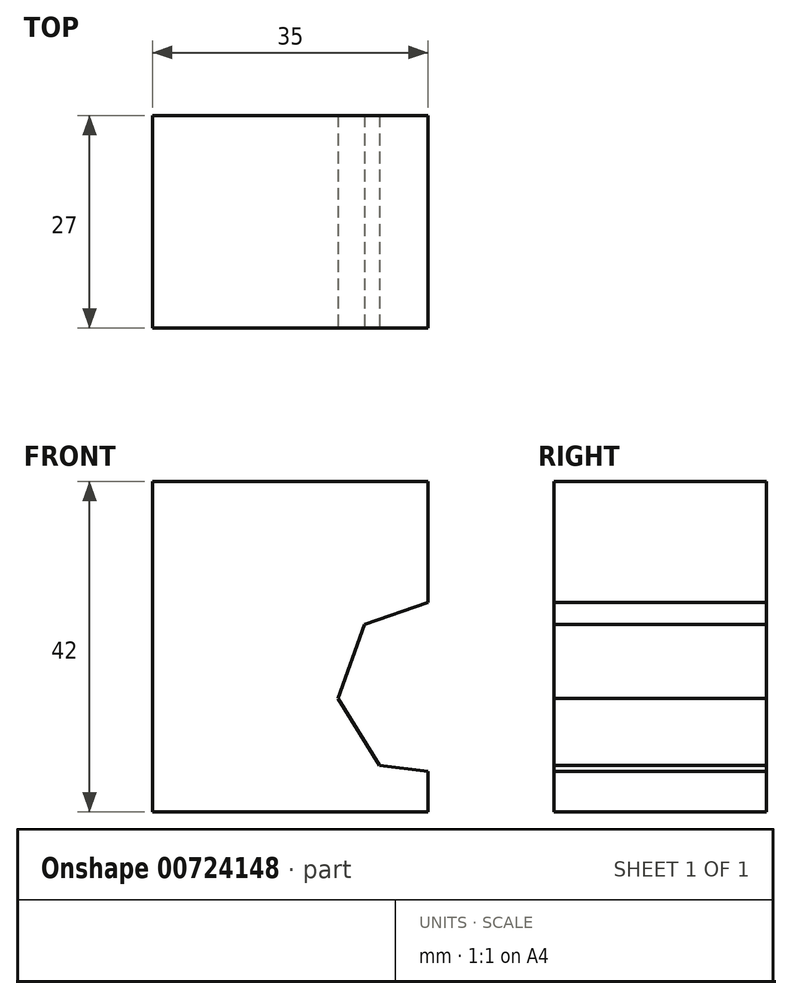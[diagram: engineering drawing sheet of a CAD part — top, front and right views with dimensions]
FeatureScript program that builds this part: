
annotation { "Feature Type Name" : "Feature", "Feature Type Description" : "" }
export const myFeature = defineFeature(function(context is Context, id is Id, definition is map)
    precondition{}
    {
        {
            var Q0;
            Q0=qCreatedBy(makeId("Front.planeOp"),FACE);
            var sketch = newSketch(context, id + "F0", { "sketchPlane" : qUnion([Q0])});
            skLineSegment(sketch, "E0.bottom", {"start": v(-35, 26.37) * mm, "end": v(0, 26.37) * mm});
            skLineSegment(sketch, "E0.top", {"start": v(-35, -15.63) * mm, "end": v(0, -15.63) * mm});
            skLineSegment(sketch, "E0.left", {"start": v(-35, 26.37) * mm, "end": v(-35, -15.63) * mm});
            skLineSegment(sketch, "E0.right", {"start": v(0, 26.37) * mm, "end": v(0, -15.63) * mm});
            skCircle(sketch, "E1.cCircle", {"center": v(0, 0) * mm, "radius": 10.38 * mm, "construction": true});
            skLineSegment(sketch, "E1.0", {"start": v(1.37, 11.44) * mm, "end": v(9.8, 6.07) * mm});
            skLineSegment(sketch, "E1.1", {"start": v(9.8, 6.07) * mm, "end": v(10.85, -3.88) * mm});
            skLineSegment(sketch, "E1.2", {"start": v(10.85, -3.88) * mm, "end": v(3.73, -10.9) * mm});
            skLineSegment(sketch, "E1.3", {"start": v(3.73, -10.9) * mm, "end": v(-6.2, -9.72) * mm});
            skLineSegment(sketch, "E1.4", {"start": v(-6.2, -9.72) * mm, "end": v(-11.46, -1.21) * mm});
            skLineSegment(sketch, "E1.5", {"start": v(-11.46, -1.21) * mm, "end": v(-8.1, 8.2) * mm});
            skLineSegment(sketch, "E1.6", {"start": v(-8.1, 8.2) * mm, "end": v(1.37, 11.44) * mm});
            skPoint(sketch, "E1.0.midPoint", {"position": v(5.58, 8.75) * mm});
            skSolve(sketch);
        }
        {
            var Q0;
            Q0=makeQuery(id+"F0.imprint","IMPRINT",FACE,{"disambiguationData":[TD([[makeQuery(id+"F0.imprint","IMPRINT",EDGE,{"derivedFrom":sQuery(id+"F0.wireOp",EDGE,"E0.bottom")}),-1.0]])]});
            extrude(context, id + "F1", {"entities" : qUnion([Q0]), "oppositeDirection" : true, "depth" : 27 * mm, "offsetDistance" : 25.4 * mm});
        }
    });
